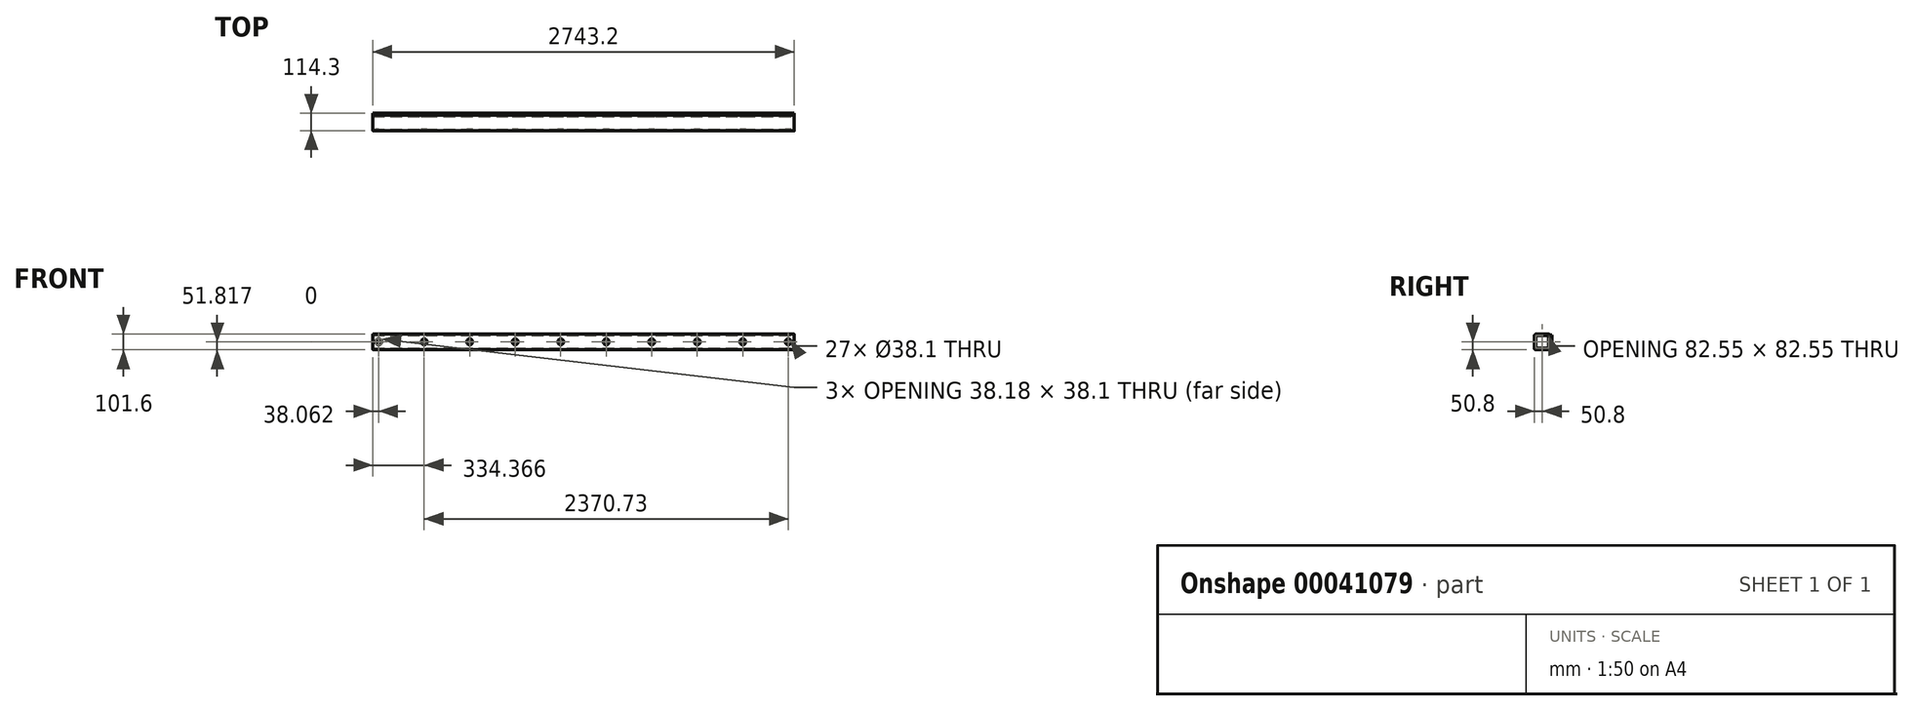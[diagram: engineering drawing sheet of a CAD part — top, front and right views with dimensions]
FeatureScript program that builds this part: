
annotation { "Feature Type Name" : "Feature", "Feature Type Description" : "" }
export const myFeature = defineFeature(function(context is Context, id is Id, definition is map)
    precondition{}
    {
        {
            var Q0;
            Q0=qCreatedBy(makeId("Right.planeOp"),FACE);
            var sketch = newSketch(context, id + "F0", { "sketchPlane" : qUnion([Q0])});
            skLineSegment(sketch, "E0.bottom", {"start": v(-8.9, 0) * mm, "end": v(-92.71, 0) * mm});
            skLineSegment(sketch, "E0.top", {"start": v(-8.9, 101.6) * mm, "end": v(-92.71, 101.6) * mm});
            skLineSegment(sketch, "E0.left", {"start": v(0, 8.9) * mm, "end": v(0, 92.71) * mm});
            skLineSegment(sketch, "E0.right", {"start": v(-101.6, 8.9) * mm, "end": v(-101.6, 92.71) * mm});
            skLineSegment(sketch, "E1.0", {"start": v(-18.42, 92.08) * mm, "end": v(-83.19, 92.08) * mm});
            skLineSegment(sketch, "E1.1", {"start": v(-9.53, 18.42) * mm, "end": v(-9.53, 83.19) * mm});
            skLineSegment(sketch, "E1.2", {"start": v(-18.42, 9.53) * mm, "end": v(-83.19, 9.53) * mm});
            skLineSegment(sketch, "E1.3", {"start": v(-92.08, 18.42) * mm, "end": v(-92.08, 83.19) * mm});
            skPoint(sketch, "E2.visualSharp", {"position": v(0, 101.6) * mm});
            skArc(sketch, "E2.filletArc", {"start": v(0, 92.71) * mm, "mid": v(-2.6, 99) * mm, "end": v(-8.9, 101.6) * mm});
            skPoint(sketch, "E3.visualSharp", {"position": v(-9.53, 92.08) * mm});
            skArc(sketch, "E3.filletArc", {"start": v(-9.53, 83.19) * mm, "mid": v(-12.13, 89.47) * mm, "end": v(-18.42, 92.08) * mm});
            skPoint(sketch, "E4.visualSharp", {"position": v(-9.53, 9.53) * mm});
            skArc(sketch, "E4.filletArc", {"start": v(-18.42, 9.53) * mm, "mid": v(-12.13, 12.13) * mm, "end": v(-9.53, 18.42) * mm});
            skPoint(sketch, "E5.visualSharp", {"position": v(-92.08, 92.08) * mm});
            skArc(sketch, "E5.filletArc", {"start": v(-83.19, 92.08) * mm, "mid": v(-89.47, 89.47) * mm, "end": v(-92.08, 83.19) * mm});
            skPoint(sketch, "E6.visualSharp", {"position": v(-92.08, 9.52) * mm});
            skArc(sketch, "E6.filletArc", {"start": v(-92.08, 18.41) * mm, "mid": v(-89.47, 12.13) * mm, "end": v(-83.19, 9.52) * mm});
            skPoint(sketch, "E7.visualSharp", {"position": v(0, 0) * mm});
            skArc(sketch, "E7.filletArc", {"start": v(-8.9, 0) * mm, "mid": v(-2.6, 2.6) * mm, "end": v(0, 8.9) * mm});
            skPoint(sketch, "E8.visualSharp", {"position": v(-101.6, 0) * mm});
            skArc(sketch, "E8.filletArc", {"start": v(-101.6, 8.9) * mm, "mid": v(-99, 2.6) * mm, "end": v(-92.71, 0) * mm});
            skPoint(sketch, "E9.visualSharp", {"position": v(-101.6, 101.6) * mm});
            skArc(sketch, "E9.filletArc", {"start": v(-92.71, 101.6) * mm, "mid": v(-99, 99) * mm, "end": v(-101.6, 92.71) * mm});
            skSolve(sketch);
        }
        {
            var Q0;
            Q0=makeQuery(id+"F0.imprint","IMPRINT",FACE,{"disambiguationData":[TD([[makeQuery(id+"F0.imprint","IMPRINT",EDGE,{"derivedFrom":sQuery(id+"F0.wireOp",EDGE,"E0.bottom")}),-1.0]])]});
            extrude(context, id + "F1", {"entities" : qUnion([Q0]), "oppositeDirection" : true, "depth" : 2743.2 * mm});
        }
        {
            var Q0;
            Q0=qCreatedBy(makeId("Right.planeOp"),FACE);
            var sketch = newSketch(context, id + "F2", { "sketchPlane" : qUnion([Q0])});
            skLineSegment(sketch, "E10.bottom", {"start": v(0, 96.27) * mm, "end": v(12.7, 96.27) * mm});
            skLineSegment(sketch, "E10.top", {"start": v(0, 7.37) * mm, "end": v(12.7, 7.37) * mm});
            skLineSegment(sketch, "E10.left", {"start": v(0, 96.27) * mm, "end": v(0, 7.37) * mm});
            skLineSegment(sketch, "E10.right", {"start": v(12.7, 96.27) * mm, "end": v(12.7, 7.37) * mm});
            skSolve(sketch);
        }
        {
            var Q0;
            Q0=makeQuery(id+"F2.imprint","IMPRINT",FACE,{"disambiguationData":[TD([[makeQuery(id+"F2.imprint","IMPRINT",EDGE,{"derivedFrom":sQuery(id+"F2.wireOp",EDGE,"E10.bottom")}),-1.0]])]});
            extrude(context, id + "F3", {"entities" : qUnion([Q0]), "oppositeDirection" : true, "depth" : 2743.2 * mm});
        }
        {
            var Q0;
            Q0=makeQuery(id+"F3.opExtrude","SWEPT_FACE",FACE,{"disambiguationData":[OSD([sQuery(id+"F2.wireOp",EDGE,"E10.right")])]});
            var sketch = newSketch(context, id + "F4", { "sketchPlane" : qUnion([Q0])});
            skCircle(sketch, "E11", {"center": v(38.1, 51.82) * mm, "radius": 19.05 * mm});
            skCircle(sketch, "E12.1.0.0", {"center": v(334.44, 51.82) * mm, "radius": 19.05 * mm});
            skCircle(sketch, "E12.2.0.0", {"center": v(630.78, 51.82) * mm, "radius": 19.05 * mm});
            skCircle(sketch, "E12.3.0.0", {"center": v(927.13, 51.82) * mm, "radius": 19.05 * mm});
            skCircle(sketch, "E12.4.0.0", {"center": v(1223.47, 51.82) * mm, "radius": 19.05 * mm});
            skCircle(sketch, "E12.5.0.0", {"center": v(1519.8, 51.82) * mm, "radius": 19.05 * mm});
            skCircle(sketch, "E12.6.0.0", {"center": v(1816.15, 51.82) * mm, "radius": 19.05 * mm});
            skCircle(sketch, "E12.7.0.0", {"center": v(2112.5, 51.82) * mm, "radius": 19.05 * mm});
            skCircle(sketch, "E12.8.0.0", {"center": v(2408.83, 51.82) * mm, "radius": 19.05 * mm});
            skCircle(sketch, "E12.9.0.0", {"center": v(2705.18, 51.82) * mm, "radius": 19.05 * mm});
            skLineSegment(sketch, "E12.direction1", {"start": v(38.1, 51.82) * mm, "end": v(334.44, 51.82) * mm, "construction": true});
            skSolve(sketch);
        }
        {
            var Q0;
            Q0=makeQuery(id+"F4.imprint","IMPRINT",FACE,{"disambiguationData":[TD([[makeQuery(id+"F4.imprint","IMPRINT",EDGE,{"derivedFrom":sQuery(id+"F4.wireOp",EDGE,"E11")}),1.0]])]});
            var Q1;
            Q1=makeQuery(id+"F4.imprint","IMPRINT",FACE,{"disambiguationData":[TD([[makeQuery(id+"F4.imprint","IMPRINT",EDGE,{"derivedFrom":sQuery(id+"F4.wireOp",EDGE,"E12.1.0.0")}),1.0]])]});
            var Q2;
            Q2=makeQuery(id+"F4.imprint","IMPRINT",FACE,{"disambiguationData":[TD([[makeQuery(id+"F4.imprint","IMPRINT",EDGE,{"derivedFrom":sQuery(id+"F4.wireOp",EDGE,"E12.2.0.0")}),1.0]])]});
            var Q3;
            Q3=makeQuery(id+"F4.imprint","IMPRINT",FACE,{"disambiguationData":[TD([[makeQuery(id+"F4.imprint","IMPRINT",EDGE,{"derivedFrom":sQuery(id+"F4.wireOp",EDGE,"E12.3.0.0")}),1.0]])]});
            var Q4;
            Q4=makeQuery(id+"F4.imprint","IMPRINT",FACE,{"disambiguationData":[TD([[makeQuery(id+"F4.imprint","IMPRINT",EDGE,{"derivedFrom":sQuery(id+"F4.wireOp",EDGE,"E12.4.0.0")}),1.0]])]});
            var Q5;
            Q5=makeQuery(id+"F4.imprint","IMPRINT",FACE,{"disambiguationData":[TD([[makeQuery(id+"F4.imprint","IMPRINT",EDGE,{"derivedFrom":sQuery(id+"F4.wireOp",EDGE,"E12.5.0.0")}),1.0]])]});
            var Q6;
            Q6=makeQuery(id+"F4.imprint","IMPRINT",FACE,{"disambiguationData":[TD([[makeQuery(id+"F4.imprint","IMPRINT",EDGE,{"derivedFrom":sQuery(id+"F4.wireOp",EDGE,"E12.6.0.0")}),1.0]])]});
            var Q7;
            Q7=makeQuery(id+"F4.imprint","IMPRINT",FACE,{"disambiguationData":[TD([[makeQuery(id+"F4.imprint","IMPRINT",EDGE,{"derivedFrom":sQuery(id+"F4.wireOp",EDGE,"E12.7.0.0")}),1.0]])]});
            var Q8;
            Q8=makeQuery(id+"F4.imprint","IMPRINT",FACE,{"disambiguationData":[TD([[makeQuery(id+"F4.imprint","IMPRINT",EDGE,{"derivedFrom":sQuery(id+"F4.wireOp",EDGE,"E12.8.0.0")}),1.0]])]});
            var Q9;
            Q9=makeQuery(id+"F4.imprint","IMPRINT",FACE,{"disambiguationData":[TD([[makeQuery(id+"F4.imprint","IMPRINT",EDGE,{"derivedFrom":sQuery(id+"F4.wireOp",EDGE,"E12.9.0.0")}),1.0]])]});
            var Q10;
            Q10=makeQuery(id+"F4.imprint","IMPRINT",FACE,{"disambiguationData":[TD([[makeQuery(id+"F4.imprint","IMPRINT",EDGE,{"derivedFrom":sQuery(id+"F4.wireOp",EDGE,"E12.10.0.0")}),1.0]])]});
            extrude(context, id + "F5", {"entities" : qUnion([Q0, Q1, Q2, Q3, Q4, Q5, Q6, Q7, Q8, Q9, Q10]), "operationType" : NewBodyOperationType.REMOVE, "endBound" : BoundingType.THROUGH_ALL, "oppositeDirection" : true, "depth" : 152.4 * mm});
        }
        {
            var Q0;
            Q0=makeQuery(id+"F1.opExtrude","SWEPT_FACE",FACE,{"disambiguationData":[OSD([sQuery(id+"F0.wireOp",EDGE,"E0.right")])]});
            var sketch = newSketch(context, id + "F6", { "sketchPlane" : qUnion([Q0])});
            skCircle(sketch, "E13.0", {"center": v(-38.1, 51.82) * mm, "radius": 19.05 * mm});
            skCircle(sketch, "E14.0", {"center": v(-334.44, 51.82) * mm, "radius": 19.05 * mm});
            skCircle(sketch, "E15.0", {"center": v(-630.78, 51.82) * mm, "radius": 19.05 * mm});
            skCircle(sketch, "E16.0", {"center": v(-927.13, 51.82) * mm, "radius": 19.05 * mm});
            skCircle(sketch, "E17.0", {"center": v(-1223.47, 51.82) * mm, "radius": 19.05 * mm});
            skCircle(sketch, "E18.0", {"center": v(-1519.8, 51.82) * mm, "radius": 19.05 * mm});
            skCircle(sketch, "E19.0", {"center": v(-1816.15, 51.82) * mm, "radius": 19.05 * mm});
            skCircle(sketch, "E20.0", {"center": v(-2112.5, 51.82) * mm, "radius": 19.05 * mm});
            skCircle(sketch, "E21.0", {"center": v(-2408.83, 51.82) * mm, "radius": 19.05 * mm});
            skCircle(sketch, "E22.0", {"center": v(-2705.18, 51.82) * mm, "radius": 19.05 * mm});
            skCircle(sketch, "E23.0", {"center": v(-2705.1, 51.82) * mm, "radius": 19.05 * mm});
            skSolve(sketch);
        }
        {
            var Q0;
            Q0 = qSketchRegion(id + "F6", true);
            extrude(context, id + "F7", {"entities" : qUnion([Q0]), "operationType" : NewBodyOperationType.REMOVE, "oppositeDirection" : true, "depth" : 254 * mm});
        }
    });
